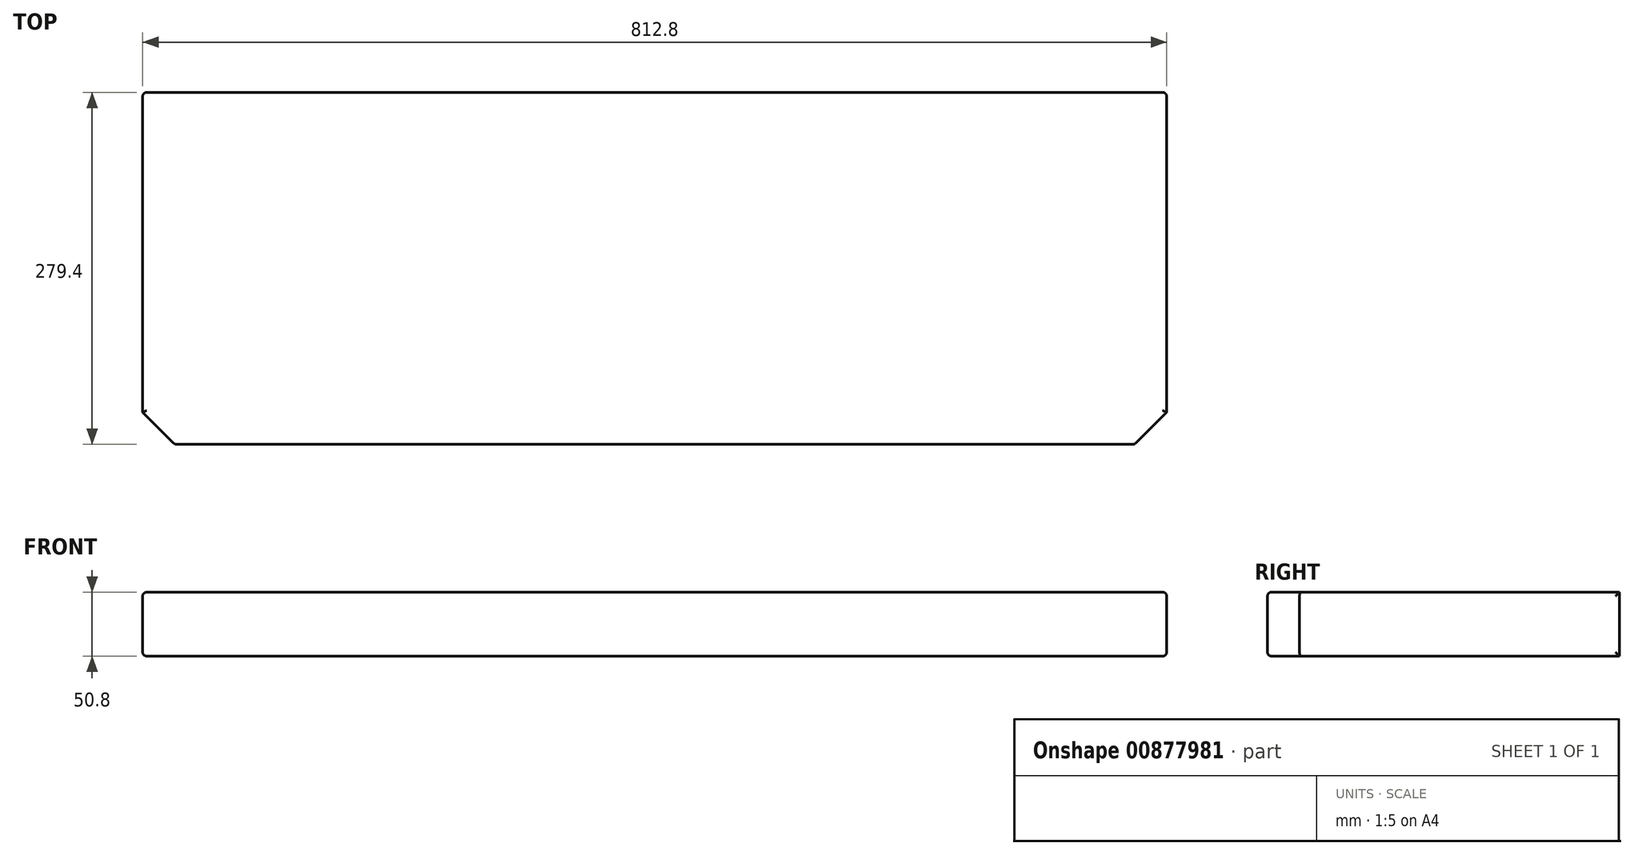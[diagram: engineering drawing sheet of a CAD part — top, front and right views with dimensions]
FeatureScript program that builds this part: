
annotation { "Feature Type Name" : "Feature", "Feature Type Description" : "" }
export const myFeature = defineFeature(function(context is Context, id is Id, definition is map)
    precondition{}
    {
        {
            var Q0;
            Q0=qCreatedBy(makeId("Top.planeOp"),FACE);
            var sketch = newSketch(context, id + "F0", { "sketchPlane" : qUnion([Q0])});
            skLineSegment(sketch, "E0.bottom", {"start": v(-812.8, 202.96) * mm, "end": v(0, 202.96) * mm});
            skLineSegment(sketch, "E0.top", {"start": v(-812.8, -76.44) * mm, "end": v(0, -76.44) * mm});
            skLineSegment(sketch, "E0.left", {"start": v(-812.8, 202.96) * mm, "end": v(-812.8, -76.44) * mm});
            skLineSegment(sketch, "E0.right", {"start": v(0, 202.96) * mm, "end": v(0, -76.44) * mm});
            skSolve(sketch);
        }
        {
            var Q0;
            Q0=makeQuery(id+"F0.imprint","IMPRINT",FACE,{"disambiguationData":[TD([[makeQuery(id+"F0.imprint","IMPRINT",EDGE,{"derivedFrom":sQuery(id+"F0.wireOp",EDGE,"E0.bottom")}),-1.0]])]});
            extrude(context, id + "F1", {"entities" : qUnion([Q0]), "depth" : 50.8 * mm, "offsetDistance" : 25.4 * mm});
        }
        {
            var Q0;
            Q0=makeQuery(id+"F1.opExtrude","SWEPT_EDGE",EDGE,{"disambiguationData":[OSD([sQuery(id+"F0.wireOp",EDGE,"E0.top"),sQuery(id+"F0.wireOp",EDGE,"E0.right")])]});
            var Q1;
            Q1=makeQuery(id+"F1.opExtrude","SWEPT_EDGE",EDGE,{"disambiguationData":[OSD([sQuery(id+"F0.wireOp",EDGE,"E0.top"),sQuery(id+"F0.wireOp",EDGE,"E0.left")])]});
            chamfer(context, id + "F2", {"entities" : qUnion([Q0, Q1]), "width" : 25.4 * mm, "tangentPropagation" : true});
        }
        {
            var Q0;
            Q0=makeQuery(id+"F1.opExtrude","SWEPT_FACE",FACE,{"disambiguationData":[OSD([sQuery(id+"F0.wireOp",EDGE,"E0.top")])]});
            var Q1;
            {var subQ0=sQuery(id+"F0.wireOp",EDGE,"E0.left");var subQ1=sQuery(id+"F0.wireOp",EDGE,"E0.top");Q1=makeQuery(id+"F2.opChamfer","BLEND_EDGE",EDGE,{"blendedFrom":[makeQuery(id+"F1.opExtrude","SWEPT_EDGE",EDGE,{"disambiguationData":[OSD([subQ1,subQ0])]}),makeQuery(id+"F1.opExtrude","CAP_FACE",FACE,{"disambiguationData":[OSD([sQuery(id+"F0.wireOp",EDGE,"E0.bottom"),subQ1,subQ0,sQuery(id+"F0.wireOp",EDGE,"E0.right")])],"isStart":false})],"blendedInto":[makeQuery(id+"F1.opExtrude","CAP_FACE",FACE,{"disambiguationData":[OSD([sQuery(id+"F0.wireOp",EDGE,"E0.bottom"),subQ1,subQ0,sQuery(id+"F0.wireOp",EDGE,"E0.right")])],"isStart":false})]});}
            var Q2;
            {var subQ0=sQuery(id+"F0.wireOp",EDGE,"E0.left");var subQ1=sQuery(id+"F0.wireOp",EDGE,"E0.top");Q2=makeQuery(id+"F2.opChamfer","BLEND_EDGE",EDGE,{"blendedFrom":[makeQuery(id+"F1.opExtrude","SWEPT_EDGE",EDGE,{"disambiguationData":[OSD([subQ1,subQ0])]}),makeQuery(id+"F1.opExtrude","CAP_FACE",FACE,{"disambiguationData":[OSD([sQuery(id+"F0.wireOp",EDGE,"E0.bottom"),subQ1,subQ0,sQuery(id+"F0.wireOp",EDGE,"E0.right")])],"isStart":true})],"blendedInto":[makeQuery(id+"F1.opExtrude","CAP_FACE",FACE,{"disambiguationData":[OSD([sQuery(id+"F0.wireOp",EDGE,"E0.bottom"),subQ1,subQ0,sQuery(id+"F0.wireOp",EDGE,"E0.right")])],"isStart":true})]});}
            var Q3;
            {var subQ0=sQuery(id+"F0.wireOp",EDGE,"E0.right");var subQ1=sQuery(id+"F0.wireOp",EDGE,"E0.top");Q3=makeQuery(id+"F2.opChamfer","BLEND_EDGE",EDGE,{"blendedFrom":[makeQuery(id+"F1.opExtrude","SWEPT_EDGE",EDGE,{"disambiguationData":[OSD([subQ1,subQ0])]}),makeQuery(id+"F1.opExtrude","CAP_FACE",FACE,{"disambiguationData":[OSD([sQuery(id+"F0.wireOp",EDGE,"E0.bottom"),subQ1,sQuery(id+"F0.wireOp",EDGE,"E0.left"),subQ0])],"isStart":true})],"blendedInto":[makeQuery(id+"F1.opExtrude","CAP_FACE",FACE,{"disambiguationData":[OSD([sQuery(id+"F0.wireOp",EDGE,"E0.bottom"),subQ1,sQuery(id+"F0.wireOp",EDGE,"E0.left"),subQ0])],"isStart":true})]});}
            var Q4;
            {var subQ0=sQuery(id+"F0.wireOp",EDGE,"E0.right");var subQ1=sQuery(id+"F0.wireOp",EDGE,"E0.top");Q4=makeQuery(id+"F2.opChamfer","BLEND_EDGE",EDGE,{"blendedFrom":[makeQuery(id+"F1.opExtrude","SWEPT_EDGE",EDGE,{"disambiguationData":[OSD([subQ1,subQ0])]}),makeQuery(id+"F1.opExtrude","CAP_FACE",FACE,{"disambiguationData":[OSD([sQuery(id+"F0.wireOp",EDGE,"E0.bottom"),subQ1,sQuery(id+"F0.wireOp",EDGE,"E0.left"),subQ0])],"isStart":false})],"blendedInto":[makeQuery(id+"F1.opExtrude","CAP_FACE",FACE,{"disambiguationData":[OSD([sQuery(id+"F0.wireOp",EDGE,"E0.bottom"),subQ1,sQuery(id+"F0.wireOp",EDGE,"E0.left"),subQ0])],"isStart":false})]});}
            var Q5;
            Q5=makeQuery(id+"F1.opExtrude","CAP_EDGE",EDGE,{"disambiguationData":[OSD([sQuery(id+"F0.wireOp",EDGE,"E0.left")])],"isStart":true});
            var Q6;
            Q6=makeQuery(id+"F1.opExtrude","CAP_EDGE",EDGE,{"disambiguationData":[OSD([sQuery(id+"F0.wireOp",EDGE,"E0.right")])],"isStart":true});
            var Q7;
            Q7=makeQuery(id+"F1.opExtrude","CAP_EDGE",EDGE,{"disambiguationData":[OSD([sQuery(id+"F0.wireOp",EDGE,"E0.right")])],"isStart":false});
            var Q8;
            Q8=makeQuery(id+"F1.opExtrude","CAP_EDGE",EDGE,{"disambiguationData":[OSD([sQuery(id+"F0.wireOp",EDGE,"E0.left")])],"isStart":false});
            var Q9;
            Q9=makeQuery(id+"F1.opExtrude","SWEPT_EDGE",EDGE,{"disambiguationData":[OSD([sQuery(id+"F0.wireOp",EDGE,"E0.bottom"),sQuery(id+"F0.wireOp",EDGE,"E0.left")])]});
            var Q10;
            Q10=makeQuery(id+"F1.opExtrude","SWEPT_EDGE",EDGE,{"disambiguationData":[OSD([sQuery(id+"F0.wireOp",EDGE,"E0.bottom"),sQuery(id+"F0.wireOp",EDGE,"E0.right")])]});
            fillet(context, id + "F3", {"entities" : qUnion([Q0, Q1, Q2, Q3, Q4, Q5, Q6, Q7, Q8, Q9, Q10]), "radius" : 3.17 * mm, "tangentPropagation" : true, "allowEdgeOverflow" : false});
        }
    });
